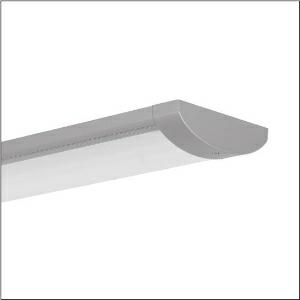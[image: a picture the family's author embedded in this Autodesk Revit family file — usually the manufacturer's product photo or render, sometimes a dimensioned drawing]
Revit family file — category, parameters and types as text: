
# Revit family: tv_20_5xa86174n0x
name_source: partatom
category: Lighting Fixtures
units: mm (PartAtom-declared; Revit-internal decimal feet)

## family parameters
Cut with Voids When Loaded = No
Host = Face
Light Source = No
Part Type = Normal
Room Calculation Point = No
Round Connector Dimension = Use Diameter
Shared = No

## types (1)
- TV 20 (1 x LED 4000K / CRI = 80 (unbekannt), 5120 lm, 4000K)
    Apparent Load = 50 VA
    CIE Flux Codes = 48 78 95 99 100
    Color Rendering = 80
    Color Temperature = 4000K
    Default Elevation = 1800 mm
    Description = TV 20, vandal-proof luminaire, primary light control with specular reflector, of aluminium, matt, primary optical cover: enclosure, of PC, frosted, light emission: direct distribution, primary light characteristic: symmetric, installation type: surface-mounted, LED, rated luminous flux: 5.120lm, luminous efficacy: 102lm/W, light colour: 840, colour temperature: 4000K, control gear: ON/OFF, mains connection: 230V, AC, 50Hz, rated input power: 50W, luminaire housing, of aluminium, coated, Siteco® metallic grey (DB 702S), with wall and ceiling fixing element, length: 1.561mm, width: 260mm, height: 70mm, mounting height: 2.5..4.0m, protection rating (complete): IP65, insulation class (complete): insulation class I (protective earthing), certification: CE, protection symbol: F, impact resistance: 2x IK10, standard: EN 60598, packaging unit: 1 piece
    Height = 70 mm
    Lamp = 1 x LED 4000K / CRI >= 80 (unbekannt)
    Lamp Light Flux = 5120 lm
    Lamp count = 1
    Length = 1561 mm
    Luminous efficacy = 102 lm/W
    Manufacturer = Siteco
    ModVariant = No
    Model = 5XA86174N0X
    Mounting Place = Ceiling
    Mounting Type = Surface mounted
    Number of Poles = 1
    OnlyDefault = Yes
    Power Factor = 1
    Product Name = TV 20
    Product group = vandal-proof luminaire
    ProductGroupID = 309
    Protection Class = Protection class I
    Protection Degree = IP 65
    RLX_Detail_Level = 1
    RLX_Emergency_Light_Flux = 0 lm
    RLX_Emergency_Type = 0
    RLX_Emergency_Type_DB = No
    RlxData = <blob elided: 25301 chars, md5=d7f9afce>
    Socket = socket
    Standby Power = 0 W
    System Light Flux = 5120 lm
    System Power = 50 W
    Type Comments = Product without accessories
    Type Image = l_1004809.jpg
    URL = http://relux.com
    VarID = ---
    Voltage = 0 V
    Weight = 0.00 kg
    Width = 260 mm

## geometry (parser evidence)
native form markers: Blend x4, Sweep x11
no freeform markers — native parametric forms only
